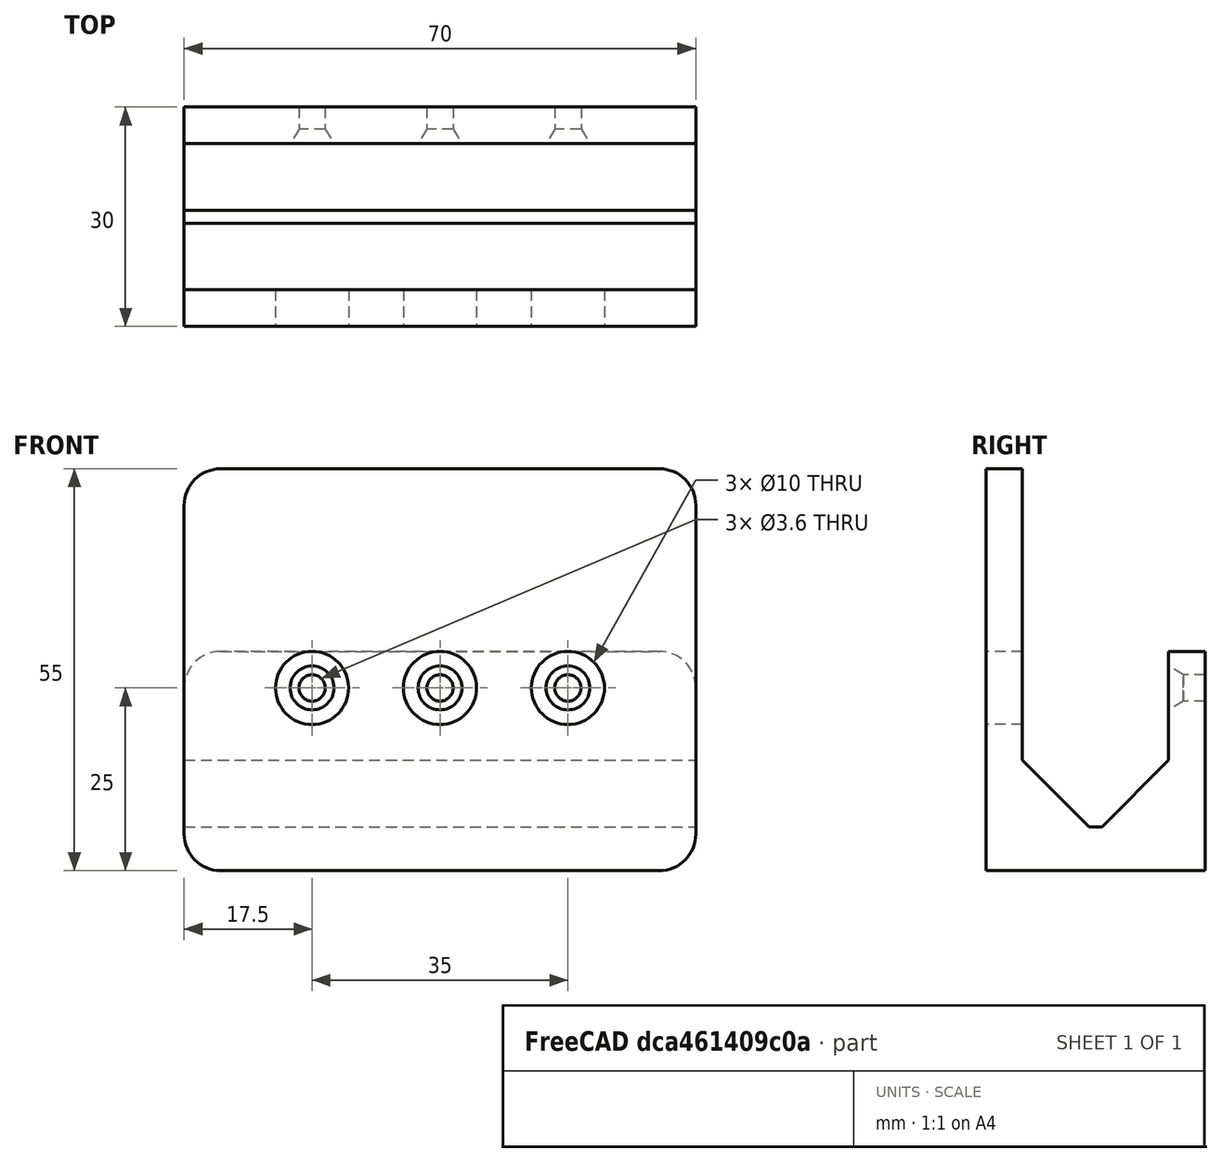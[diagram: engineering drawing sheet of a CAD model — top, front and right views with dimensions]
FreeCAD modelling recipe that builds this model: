
FCSTD DOCUMENT  (FreeCAD 0.18.4R)
Label: wire_hanger
License: FreeArt
LicenseURL: http://artlibre.org/licence/lal
objects: Part::Box×3, Part::Cylinder×2, Part::MultiFuse×2, Part::Fillet×2, Part::Cut×2, Spreadsheet::Sheet×1, Part::Cone×1, Part::FeaturePython×1, Part::Chamfer×1
note: 14 computed .brp shape members not serialized (recipe doc carries the construction recipe); baked Part::Feature solids carry a one-line shape summary decoded from their .brp

FEATURE [Part::Box] Box  label="external half cube"
  AttacherType = Attacher::AttachEngine3D
  Height = 55
  Length = 70
  Width = 15
  expr: Height = p.size_z + p.wall
  expr: Width = p.size_y / 2 + p.wall
  expr: Length = p.size_x
FEATURE [Spreadsheet::Sheet] Spreadsheet  label="p"
  cells = A1=size_x; B1(size_x)=70; A2=size_y; B2(size_y)=20; A3=size_z; B3(size_z)=50; A4=wall; B4(wall)=5; A5=bottom_wall; B5(bottom_wall)=6; A6=hole_r; B6(hole_r)=1.8; A7=head_r; B7(head_r)=3; A8=head_z; B8(head_z)=2; A9=screw_driver_hole_r; B9(screw_driver_hole_r)=5
FEATURE [Part::Box] Box001  label="internal cube"
  AttacherType = Attacher::AttachEngine3D
  Height = 50
  Length = 70
  Placement = pos=(0,5,6) rot=(0,0,1;0rad)
  Width = 20
  expr: Placement.Base.y = p.wall
  expr: Placement.Base.z = p.bottom_wall
  expr: Height = p.size_z
  expr: Width = p.size_y
  expr: Length = p.size_x
FEATURE [Part::Cylinder] Cylinder  label="screw driver hole"
  Angle = 360
  AttacherType = Attacher::AttachEngine3D
  Height = 30
  Placement = pos=(0,0,7) rot=(0,0,1;0rad)
  Radius = 5
  expr: Height = p.size_y + p.wall * 2
  expr: Placement.Base.z = p.wall + p.head_z
  expr: Radius = p.screw_driver_hole_r
FEATURE [Part::Cylinder] Cylinder001  label="screw hole"
  Angle = 360
  AttacherType = Attacher::AttachEngine3D
  Height = 5
  Radius = 1.8
  expr: Height = p.wall
  expr: Radius = p.hole_r
FEATURE [Part::Cone] Cone  label="screw head cone"
  Angle = 360
  AttacherType = Attacher::AttachEngine3D
  Height = 2
  Placement = pos=(0,0,5) rot=(0,0,1;0rad)
  Radius1 = 1.8
  Radius2 = 3
  expr: Radius1 = p.hole_r
  expr: Placement.Base.z = p.wall
  expr: Height = p.head_z
  expr: Radius2 = p.head_r
FEATURE [Part::MultiFuse] Fusion  label="hole fusion"
  Shapes = -> [Cone,Cylinder001,Cylinder]
FEATURE [Part::FeaturePython] Array  label="hole array"  # Draft array (typed FeaturePython)
  Angle = 360
  ArrayType = 0
  Axis = (0,0,1)
  Base = -> Fusion
  Center = (0,0,0)
  Fuse = false
  IntervalAxis = (0,0,0)
  IntervalX = (17.5,0,0)
  IntervalY = (0,1,0)
  IntervalZ = (0,0,1)
  NumberPolar = 1
  NumberX = 3
  NumberY = 1
  NumberZ = 1
  Placement = pos=(17.5,32,25) rot=(1,0,0;1.5708rad)
  expr: Placement.Base.x = p.size_x / 4
  expr: Placement.Base.y = p.size_y + 2 * p.wall + p.head_z
  expr: Placement.Base.z = p.size_z / 2
  expr: IntervalX.x = p.size_x / 4
FEATURE [Part::Box] Box002  label="external hole side half cube"
  AttacherType = Attacher::AttachEngine3D
  Height = 30
  Length = 70
  Placement = pos=(0,15,0) rot=(0,0,1;0rad)
  Width = 15
  expr: Placement.Base.y = p.size_y / 2 + p.wall
  expr: Height = p.size_z / 2 + p.wall
  expr: Width = p.size_y / 2 + p.wall
  expr: Length = p.size_x
FEATURE [Part::Fillet] Fillet001  label="external half fillet"
  Base = -> Box
  Edges = 4 edges r=5: [Edge2,Edge4,Edge6,Edge8]
FEATURE [Part::Fillet] Fillet002  label="external hole side half fillet"
  Base = -> Box002
  Edges = 4 edges r=5: [Edge2,Edge4,Edge6,Edge8]
FEATURE [Part::MultiFuse] Fusion001  label="external half cube fusion"
  Shapes = -> [Fillet001,Fillet002]
FEATURE [Part::Cut] Cut  label="wire hanger cut"
  Base = -> Fusion001
  Tool = -> Box001
FEATURE [Part::Chamfer] Chamfer  label="wire hanger chamfer"
  Base = -> Cut
  Edges = 2 edges r=9.1: [Edge19,Edge21]
FEATURE [Part::Cut] Cut001  label="wire hanger cut001"
  Base = -> Chamfer
  Tool = -> Array
